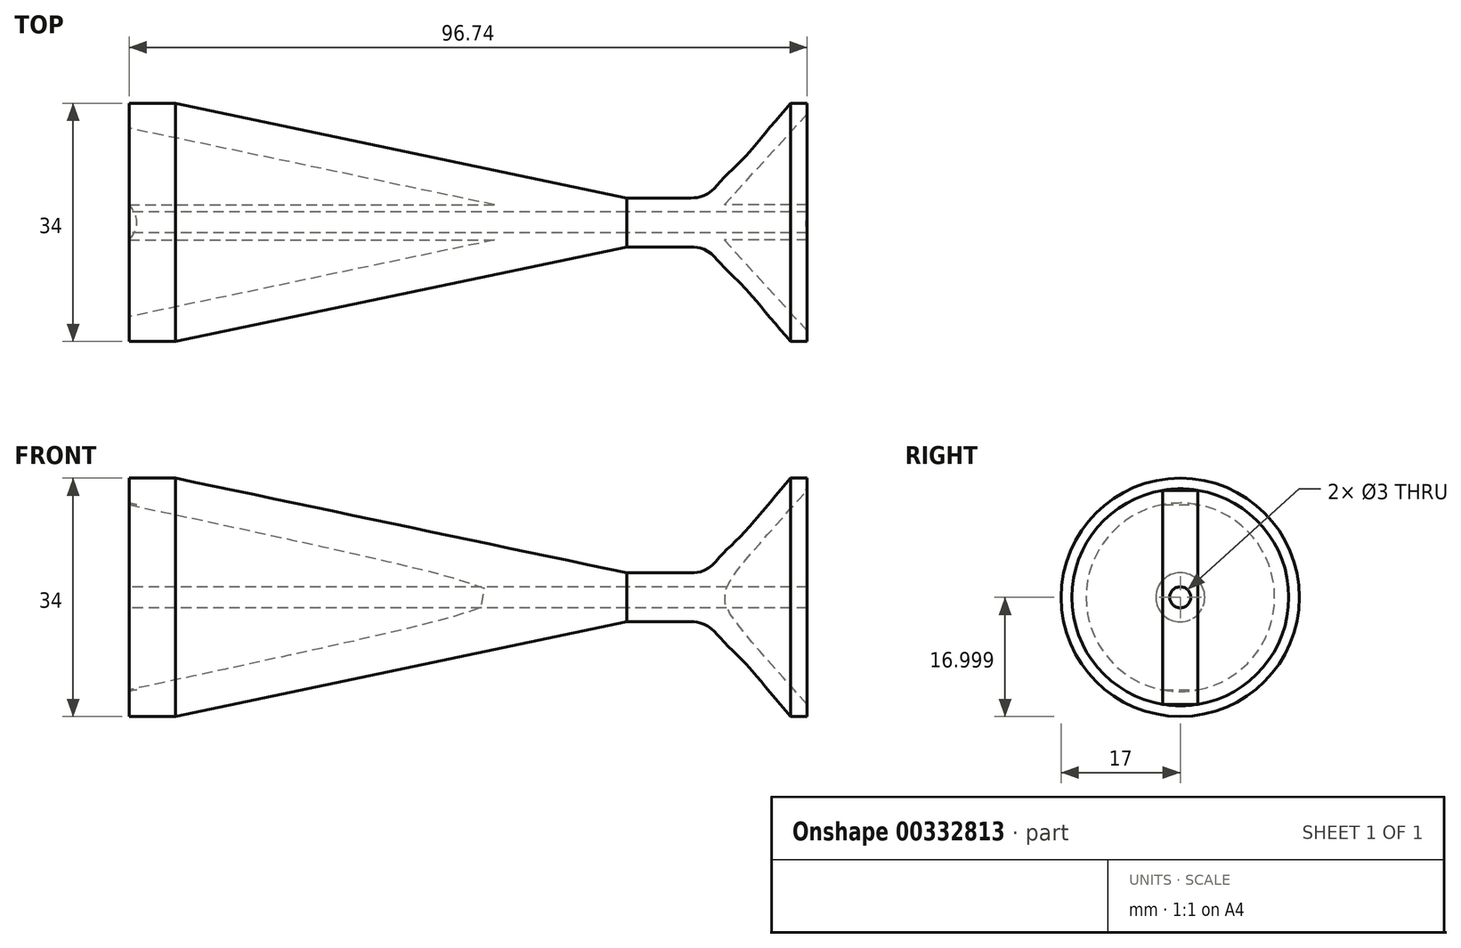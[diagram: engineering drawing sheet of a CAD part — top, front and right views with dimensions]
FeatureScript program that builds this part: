
annotation { "Feature Type Name" : "Feature", "Feature Type Description" : "" }
export const myFeature = defineFeature(function(context is Context, id is Id, definition is map)
    precondition{}
    {
        {
            var Q0;
            Q0=qCreatedBy(makeId("Front.planeOp"),FACE);
            var sketch = newSketch(context, id + "F0", { "sketchPlane" : qUnion([Q0])});
            skLineSegment(sketch, "E0", {"start": v(268.4, -81.24) * mm, "end": v(268.4, -61.24) * mm, "construction": true});
            skFitSpline(sketch, "E1", {"points": [v(268.4, -61.24) * mm, v(266.6, -63.53) * mm, v(262.84, -67.99) * mm, v(258.92, -72.52) * mm, v(256.39, -74.97) * mm, v(254.47, -76.97) * mm, v(252.85, -77.66) * mm, v(251.78, -77.74) * mm], "startDerivative": vector(-11.74, -15.5) * mm, "endDerivative": vector(-12.31, -0.08) * mm});
            skLineSegment(sketch, "E2", {"start": v(251.78, -77.74) * mm, "end": v(242.64, -77.74) * mm});
            skLineSegment(sketch, "E3", {"start": v(242.64, -77.74) * mm, "end": v(242.64, -81.24) * mm});
            skLineSegment(sketch, "E4", {"start": v(242.64, -81.24) * mm, "end": v(254.26, -81.24) * mm});
            skLineSegment(sketch, "E5", {"start": v(254.26, -81.24) * mm, "end": v(268.4, -65.76) * mm});
            skLineSegment(sketch, "E6", {"start": v(268.4, -65.76) * mm, "end": v(268.4, -61.24) * mm});
            skSolve(sketch);
        }
        {
            var Q0;
            Q0 = qSketchRegion(id + "F0", true);
            var Q1;
            Q1=sQuery(id+"F0.wireOp",EDGE,"E4");
            revolve(context, id + "F1", {"entities" : qUnion([Q0]), "axis" : qUnion([Q1]), "revolveType" : RevolveType.FULL});
        }
        {
            var Q0;
            Q0=qCreatedBy(makeId("Front.planeOp"),FACE);
            var sketch = newSketch(context, id + "F2", { "sketchPlane" : qUnion([Q0])});
            skLineSegment(sketch, "E7", {"start": v(171.65, -62.85) * mm, "end": v(242.64, -77.74) * mm});
            skLineSegment(sketch, "E8", {"start": v(242.64, -77.74) * mm, "end": v(242.64, -81.24) * mm});
            skLineSegment(sketch, "E9", {"start": v(242.64, -81.24) * mm, "end": v(235.75, -81.24) * mm});
            skLineSegment(sketch, "E10", {"start": v(235.75, -81.24) * mm, "end": v(171.65, -67.8) * mm});
            skLineSegment(sketch, "E11", {"start": v(171.65, -67.8) * mm, "end": v(171.65, -62.85) * mm});
            skSolve(sketch);
        }
        {
            var Q0;
            Q0 = qSketchRegion(id + "F2", true);
            var Q1;
            Q1=sQuery(id+"F2.wireOp",EDGE,"E9");
            revolve(context, id + "F3", {"entities" : qUnion([Q0]), "axis" : qUnion([Q1]), "revolveType" : RevolveType.FULL});
        }
        {
            var Q0;
            Q0=makeQuery(id+"F1.opRevolve","SWEPT_FACE",FACE,{"disambiguationData":[OSD([sQuery(id+"F0.wireOp",EDGE,"E6")])]});
            var sketch = newSketch(context, id + "F4", { "sketchPlane" : qUnion([Q0])});
            skPoint(sketch, "E12.middle", {"position": v(0, -81.24) * mm});
            skLineSegment(sketch, "E13.bottom", {"start": v(2.5, -96.51) * mm, "end": v(-2.5, -96.51) * mm});
            skLineSegment(sketch, "E13.top", {"start": v(2.5, -65.97) * mm, "end": v(-2.5, -65.97) * mm});
            skLineSegment(sketch, "E13.left", {"start": v(2.5, -96.51) * mm, "end": v(2.5, -65.97) * mm});
            skLineSegment(sketch, "E13.right", {"start": v(-2.5, -96.51) * mm, "end": v(-2.5, -65.97) * mm});
            skSolve(sketch);
        }
        {
            var Q0;
            Q0 = qSketchRegion(id + "F4", true);
            extrude(context, id + "F5", {"entities" : qUnion([Q0]), "operationType" : NewBodyOperationType.ADD, "endBound" : BoundingType.UP_TO_NEXT, "oppositeDirection" : true, "depth" : 25 * mm});
        }
        {
            var Q0;
            Q0=makeQuery(id+"F3.opRevolve","SWEPT_FACE",FACE,{"disambiguationData":[OSD([sQuery(id+"F2.wireOp",EDGE,"E11")])]});
            var sketch = newSketch(context, id + "F6", { "sketchPlane" : qUnion([Q0])});
            skLineSegment(sketch, "E14.bottom", {"start": v(2.5, -68.03) * mm, "end": v(-2.5, -68.03) * mm});
            skLineSegment(sketch, "E14.top", {"start": v(2.5, -94.45) * mm, "end": v(-2.5, -94.45) * mm});
            skLineSegment(sketch, "E14.left", {"start": v(2.5, -68.03) * mm, "end": v(2.5, -94.45) * mm});
            skLineSegment(sketch, "E14.right", {"start": v(-2.5, -68.03) * mm, "end": v(-2.5, -94.45) * mm});
            skPoint(sketch, "E14.middle", {"position": v(0, -81.24) * mm});
            skSolve(sketch);
        }
        {
            var Q0;
            Q0 = qSketchRegion(id + "F6", true);
            extrude(context, id + "F7", {"entities" : qUnion([Q0]), "operationType" : NewBodyOperationType.ADD, "endBound" : BoundingType.UP_TO_NEXT, "oppositeDirection" : true, "depth" : 25 * mm});
        }
        {
            var Q0;
            Q0=makeQuery(id+"F7.opExtrude","CAP_FACE",FACE,{"disambiguationData":[OSD([sQuery(id+"F6.wireOp",EDGE,"E14.bottom"),sQuery(id+"F6.wireOp",EDGE,"E14.top"),sQuery(id+"F6.wireOp",EDGE,"E14.left"),sQuery(id+"F6.wireOp",EDGE,"E14.right")])],"isStart":true});
            var sketch = newSketch(context, id + "F8", { "sketchPlane" : qUnion([Q0])});
            skCircle(sketch, "E15", {"center": v(0, -81.24) * mm, "radius": 1.5 * mm});
            skPoint(sketch, "E15.centerSnap0", {"position": v(2.5, -81.24) * mm});
            skPoint(sketch, "E15.centerSnap1", {"position": v(0, -68.03) * mm});
            skSolve(sketch);
        }
        {
            var Q0;
            Q0 = qSketchRegion(id + "F8", true);
            extrude(context, id + "F9", {"entities" : qUnion([Q0]), "operationType" : NewBodyOperationType.REMOVE, "endBound" : BoundingType.THROUGH_ALL, "oppositeDirection" : true, "depth" : 25 * mm});
        }
        {
            var Q0;
            Q0=makeQuery(id+"F1.opRevolve","SWEPT_FACE",FACE,{"disambiguationData":[OSD([sQuery(id+"F0.wireOp",EDGE,"E6")])]});
            var sketch = newSketch(context, id + "F10", { "sketchPlane" : qUnion([Q0])});
            skCircle(sketch, "E16", {"center": v(0, -81.24) * mm, "radius": 1.5 * mm});
            skSolve(sketch);
        }
        {
            var Q0;
            Q0 = qSketchRegion(id + "F10", true);
            extrude(context, id + "F11", {"entities" : qUnion([Q0]), "operationType" : NewBodyOperationType.REMOVE, "endBound" : BoundingType.THROUGH_ALL, "oppositeDirection" : true, "depth" : 25 * mm});
        }
        {
            var Q0;
            Q0=makeQuery(id+"F1.opRevolve","SWEPT_FACE",FACE,{"disambiguationData":[OSD([sQuery(id+"F0.wireOp",EDGE,"E6")])]});
            var sketch = newSketch(context, id + "F12", { "sketchPlane" : qUnion([Q0])});
            skCircle(sketch, "E17", {"center": v(0, -81.24) * mm, "radius": 17 * mm});
            skCircle(sketch, "E18", {"center": v(0, -81.24) * mm, "radius": 26.7 * mm});
            skSolve(sketch);
        }
        {
            var Q0;
            Q0 = qSketchRegion(id + "F12", true);
            extrude(context, id + "F13", {"entities" : qUnion([Q0]), "operationType" : NewBodyOperationType.REMOVE, "endBound" : BoundingType.THROUGH_ALL, "oppositeDirection" : true, "depth" : 25 * mm});
        }
    });
